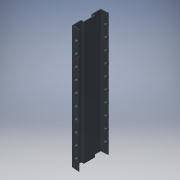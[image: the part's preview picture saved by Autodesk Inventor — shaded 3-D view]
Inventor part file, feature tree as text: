
AUTODESK INVENTOR PART (.ipt)
format: ipt  version: 2016 (Build 200138000, 138)  size: 160,256 bytes
history: native  units: mm
features: other x7, sketch x3, revolve x2, pattern_linear x2, extrude x1
ambient origin geometry x8: Origin, YZ Plane, XZ Plane, XY Plane, X Axis, Y Axis, Z Axis, Center Point
bodies: Solid1 (feature_tree)
feature tree (15):
  extrude  "Extrusion1"  TaperAngle=360.0deg  [1 undecoded]
  revolve  "Revolution1"  Angle=360.0deg
  pattern_linear  "Rectangular Pattern1"  Count1=10 Spacing1=11.7mm
  revolve  "Revolution2"  [1 undecoded]
  pattern_linear  "Rectangular Pattern2"  [2 undecoded]
  other  "to_rail_XY"
  other  "to_rail_YZ"
  other  "to_rail_ZX"
  other  "to_rail_X"
  other  "to_rail_Y"
  other  "to_rail_Z"
  other  "to_rail_Center"
  sketch  "Sketch_1"  dims[d0=127.0mm d1=0.0mm d2=360.0deg]
  sketch  "Sketch_2"  dims[d3=100.0mm d5=11.7mm d6=10.0mm d8=0.0mm d9=360.0deg d10=100.0mm d12=11.7mm d13=10.0mm d15=0.0mm]
  sketch  "Sketch_4"
note: 4 required parameter values undecoded (feature->parameter linkage not recoverable at this tier; creation-order binding heuristic only, values carry confidence <= 0.55)
